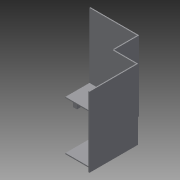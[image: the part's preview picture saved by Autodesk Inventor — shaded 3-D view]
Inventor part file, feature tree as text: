
AUTODESK INVENTOR PART (.ipt)
format: ipt  version: 2014 (Build 180170000, 170)  size: 200,704 bytes
history: native  units: in
note: dims shown in document units (in); Inventor stores cm internally (conversion verified against a paired STEP export)
features: extrude x12, sketch x12
ambient origin geometry x8: Origin, YZ Plane, XZ Plane, XY Plane, X Axis, Y Axis, Z Axis, Center Point
bodies: Solid1 (feature_tree)
feature tree (24):
  extrude  "Extrusion1"  Depth=23.5in
  extrude  "Extrusion2"  Depth=47.5in
  extrude  "Extrusion3"  Depth=64.5in
  extrude  "Extrusion4"  Depth=64.5in
  extrude  "Extrusion5"  Depth=1.0in TaperAngle=0.0deg
  extrude  "Extrusion6"  Depth=1.0in TaperAngle=0.0deg
  extrude  "Extrusion7"  Depth=4.0in
  extrude  "Extrusion8"  Depth=4.0in TaperAngle=0.0deg
  extrude  "Extrusion9"  Depth=4.0in
  extrude  "Extrusion10"  Depth=1.0in TaperAngle=0.0deg
  extrude  "Extrusion11"  Depth=1.0in TaperAngle=0.0deg
  extrude  "Extrusion12"  Depth=1.0in TaperAngle=0.0deg
  sketch  "Sketch1"  dims[d0=47.5in d1=23.5in]
  sketch  "Sketch2"  dims[d2=23.5in d3=47.5in]
  sketch  "Sketch3"  dims[d4=1.0in d5=0.0in d6=64.5in]
  sketch  "Sketch4"  dims[d7=1.0in d8=0.0in d9=64.5in]
  sketch  "Sketch5"  dims[d10=1.0in d11=0.0in d12=1.0in d13=0.0in]
  sketch  "Sketch6"  dims[d14=64.5in d15=1.0in d16=0.0in]
  sketch  "Sketch7"  dims[d17=4.0in d18=4.0in]
  sketch  "Sketch8"  dims[d19=4.0in d20=0.0in d21=0.25in d22=0.0in]
  sketch  "Sketch9"  dims[d23=4.0in d24=4.0in]
  sketch  "Sketch10"  dims[d25=4.0in d26=0.0in d27=1.0in d28=0.0in]
  sketch  "Sketch11"  dims[d29=4.0in d30=1.0in d31=0.0in]
  sketch  "Sketch12"  dims[d32=1.0in d33=0.0in d34=1.0in d35=0.0in]
